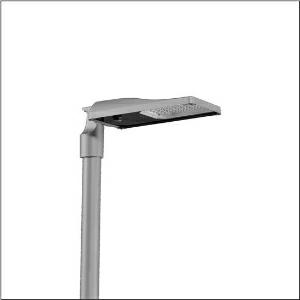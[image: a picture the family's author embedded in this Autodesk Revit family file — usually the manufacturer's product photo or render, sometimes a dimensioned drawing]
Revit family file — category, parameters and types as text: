
# Revit family: streetlight_sl_31_mini___st1_0a_5xh2d31r08ha_940f
name_source: partatom
category: Lighting Fixtures
units: mm (PartAtom-declared; Revit-internal decimal feet)

## family parameters
Cut with Voids When Loaded = No
Host = Face
Light Source = No
Part Type = Normal
Room Calculation Point = No
Round Connector Dimension = Use Diameter
Shared = No

## types (1)
- --- (1 x LED, 9230 lm, 68.3 W, 3000K)
    Apparent Load = 68 VA
    CIE Flux Codes = 37 72 97 100 100
    Color Rendering = 70
    Color Temperature = 3000K
    Default Elevation = 1800 mm
    Description = Streetlight SL 31 mini D4i, Desk-Remote mast luminaire for post-top, side-entry; light control with lens of PMMA; light distribution: ST1.0a, direct asymmetric distribution, for standard-compliant lighting for roads and squares; LED: luminous flux: 9.230lm, light colour: 730, colour temperature: 3000K; luminous efficacy: 135,3lm/W; control: pre-setting: logarithmic dimming characteristic, flexible luminous flux parameterisation, time-dependent luminous flux control, constant luminous flux control, power reduction, intelligent temperature release in ECG and LED module, overheat protection; luminaire housing, of diecast aluminium, Siteco® metallic grey (DB 702S), corrosivity category C5 high according to DIN EN ISO 12944; cover of toughened safety glass, transparent, mast flange of diecast aluminium, Siteco® metallic grey (DB 702S), spigot size: 76/60mm, mast flange included unmounted; with cable H07RN-F 2x 1.5mm², cable length: 8,5m, connection cable pre-assembled; mains connection: 220..240V, AC, 50/60Hz; power consumption (at start of service life): 68,2W / (at end of service life): 74,4W / (with reduced operation 50%): 29,7W; protection rating (complete): IP66; insulation class (complete): insulation class II (safety insulation); impact resistance: IK09; certification: CE, ENEC, ENEC+, VDE, UKCA, ZD4i; permissible operating ambient temperature for outdoor applications: -40..+50°C; packaging unit: 1 piece

Light Distribution: ST1.0a
    Height = 76 mm
    Lamp = 1 x LED
    Lamp Light Flux = 9230 lm
    Lamp Power = 68.3 W
    Lamp count = 1
    Length = 547 mm
    Luminous efficacy = 135 lm/W
    Manufacturer = Siteco
    ModVariant = No
    Model = 5XH2D31R08HA
    Number of Poles = 1
    OnlyDefault = Yes
    Power Factor = 1
    Product Name = Streetlight SL 31 mini | ST1.0a
    Product group = mast luminaire | pylon top
    ProductGroupID = 6100
    Protection Class = Protection class II
    Protection Degree = IP 66
    RLX_Detail_Level = 1
    RLX_Emergency_Light_Flux = 0 lm
    RLX_Emergency_Type = 0
    RLX_Emergency_Type_DB = No
    RlxData = <blob elided: 24197 chars, md5=046aa537>
    Socket = socket
    Standby Power = 0 W
    System Light Flux = 9230 lm
    System Power = 68 W
    Type Comments = factory setting: luminous flux: 100 % | dim-lin: 254 | 692 mA
    Type Image = l_1300328.jpg
    URL = http://relux.com
    VarID = @adj_002957
    Voltage = 0 V
    Weight = 0.00 kg
    Width = 265 mm

## geometry (parser evidence)
native form markers: Blend x4, Sweep x11
no freeform markers — native parametric forms only
